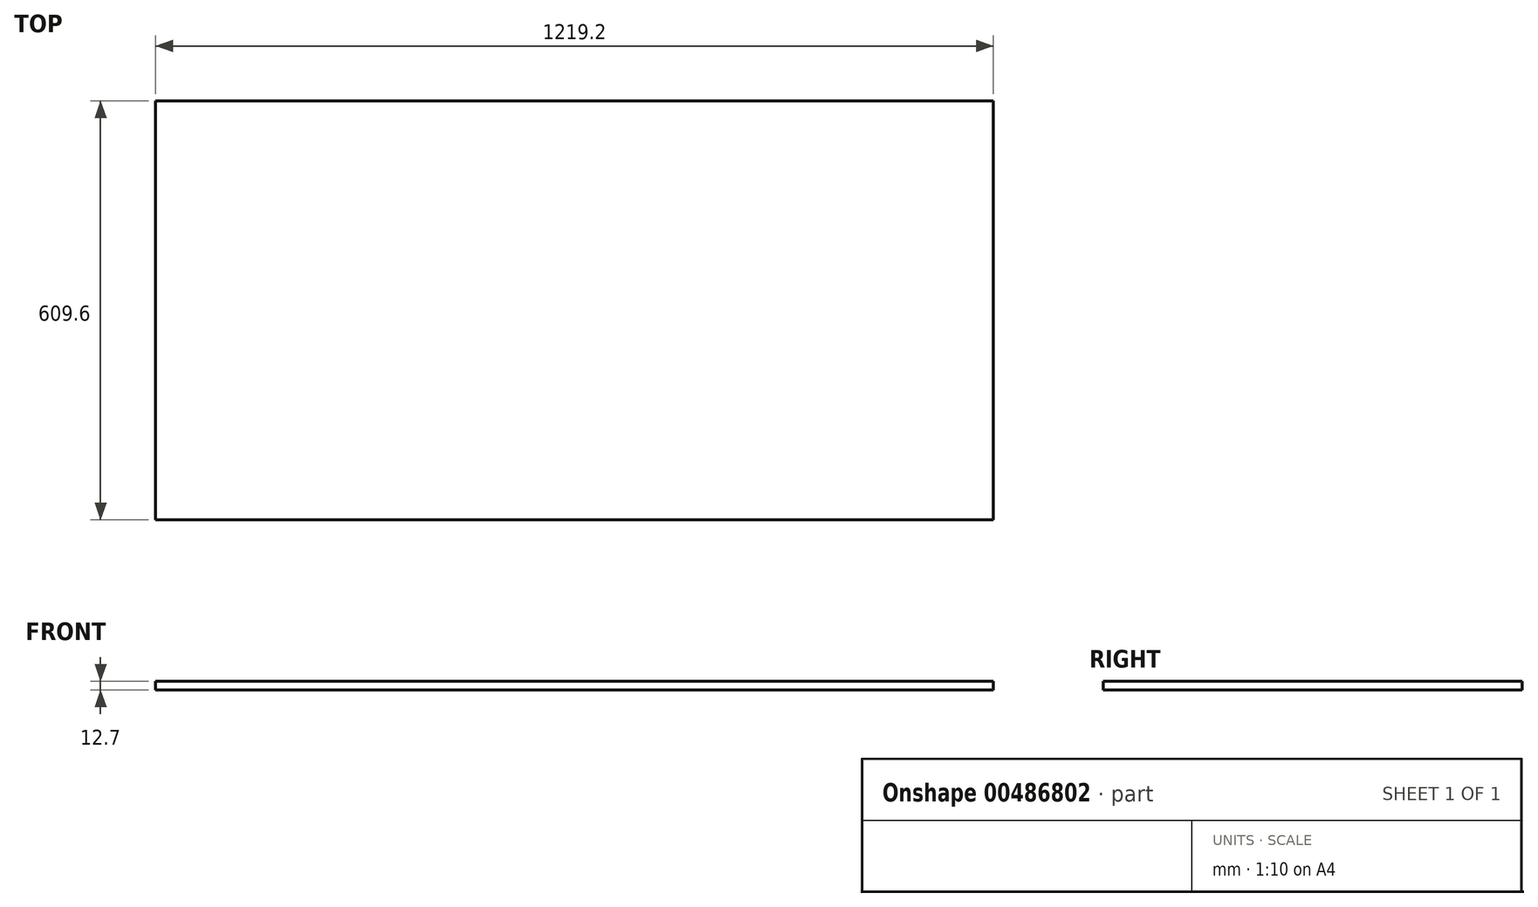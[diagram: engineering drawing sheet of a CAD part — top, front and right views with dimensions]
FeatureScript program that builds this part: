
annotation { "Feature Type Name" : "Feature", "Feature Type Description" : "" }
export const myFeature = defineFeature(function(context is Context, id is Id, definition is map)
    precondition{}
    {
        {
            var Q0;
            Q0=qCreatedBy(makeId("Top.planeOp"),FACE);
            var sketch = newSketch(context, id + "F0", { "sketchPlane" : qUnion([Q0])});
            skLineSegment(sketch, "E0.bottom", {"start": v(609.6, -304.8) * mm, "end": v(-609.6, -304.8) * mm});
            skLineSegment(sketch, "E0.top", {"start": v(609.6, 304.8) * mm, "end": v(-609.6, 304.8) * mm});
            skLineSegment(sketch, "E0.left", {"start": v(609.6, -304.8) * mm, "end": v(609.6, 304.8) * mm});
            skLineSegment(sketch, "E0.right", {"start": v(-609.6, -304.8) * mm, "end": v(-609.6, 304.8) * mm});
            skPoint(sketch, "E0.middle", {"position": v(0, 0) * mm});
            skSolve(sketch);
        }
        {
            var Q0;
            Q0=makeQuery(id+"F0.imprint","IMPRINT",FACE,{"disambiguationData":[TD([[makeQuery(id+"F0.imprint","IMPRINT",EDGE,{"derivedFrom":sQuery(id+"F0.wireOp",EDGE,"E0.bottom")}),-1.0]])]});
            extrude(context, id + "F1", {"entities" : qUnion([Q0]), "depth" : 12.7 * mm});
        }
    });
